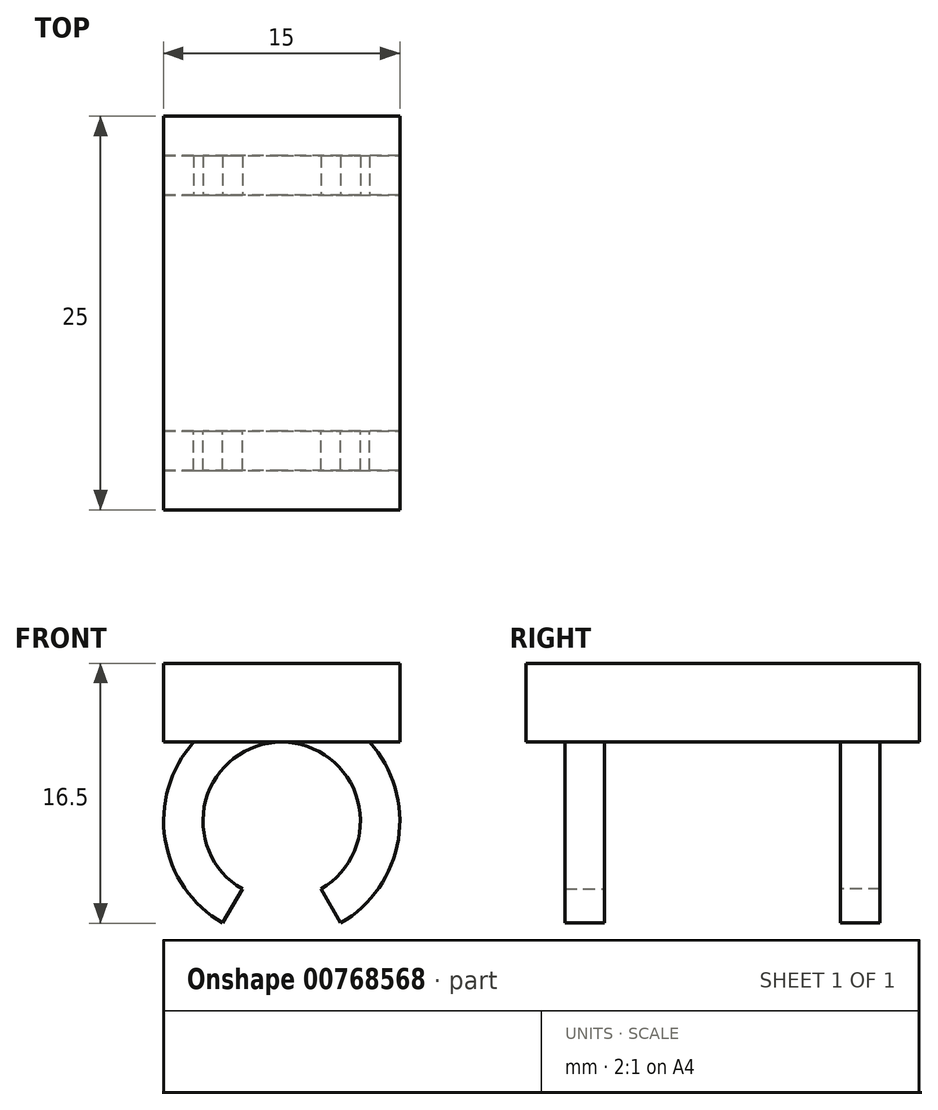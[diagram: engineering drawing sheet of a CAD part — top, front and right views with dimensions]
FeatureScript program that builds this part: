
annotation { "Feature Type Name" : "Feature", "Feature Type Description" : "" }
export const myFeature = defineFeature(function(context is Context, id is Id, definition is map)
    precondition{}
    {
        {
            var Q0;
            Q0=qCreatedBy(makeId("Front.planeOp"),FACE);
            var sketch = newSketch(context, id + "F0", { "sketchPlane" : qUnion([Q0])});
            skLineSegment(sketch, "E0.bottom", {"start": v(-7.5, 2.5) * mm, "end": v(7.5, 2.5) * mm});
            skLineSegment(sketch, "E0.top", {"start": v(-7.5, -2.5) * mm, "end": v(7.5, -2.5) * mm});
            skLineSegment(sketch, "E0.left", {"start": v(-7.5, 2.5) * mm, "end": v(-7.5, -2.5) * mm});
            skLineSegment(sketch, "E0.right", {"start": v(7.5, 2.5) * mm, "end": v(7.5, -2.5) * mm});
            skPoint(sketch, "E0.middle", {"position": v(0, 0) * mm});
            skCircle(sketch, "E1", {"center": v(0, -7.5) * mm, "radius": 5 * mm});
            skCircle(sketch, "E2", {"center": v(0, -7.5) * mm, "radius": 7.5 * mm});
            skLineSegment(sketch, "E3", {"start": v(2.5, -11.83) * mm, "end": v(3.75, -14) * mm});
            skLineSegment(sketch, "E4", {"start": v(-2.5, -11.83) * mm, "end": v(-3.75, -14) * mm});
            skSolve(sketch);
        }
        {
            var Q0;
            Q0=makeQuery(id+"F0.imprint","IMPRINT",FACE,{"disambiguationData":[TD([[makeQuery(id+"F0.imprint","IMPRINT",EDGE,{"derivedFrom":sQuery(id+"F0.wireOp",EDGE,"E0.bottom")}),-1.0]])]});
            var Q1;
            {var subQ0=sQuery(id+"F0.wireOp",EDGE,"E2");var subQ1=sQuery(id+"F0.wireOp",EDGE,"E0.top");var subQ2=makeQuery(id+"F0.imprint","INTERSECT",VERTEX,{"disambiguationData":[OD(0.0)],"derivedFrom":[subQ1,subQ0]});Q1=makeQuery(id+"F0.imprint","IMPRINT",FACE,{"disambiguationData":[TD([[makeQuery(id+"F0.imprint","IMPRINT",EDGE,{"disambiguationData":[TD([[subQ2,-1.0]])],"derivedFrom":subQ1}),1.0]])]});}
            extrude(context, id + "F1", {"entities" : qUnion([Q0, Q1]), "endBound" : BoundingType.SYMMETRIC, "depth" : 25 * mm, "offsetDistance" : 25 * mm});
        }
        {
            var Q0;
            {var subQ5=sQuery(id+"F0.wireOp",EDGE,"E4");Q0=makeQuery(id+"F0.imprint","IMPRINT",FACE,{"disambiguationData":[TD([[makeQuery(id+"F0.imprint","IMPRINT",EDGE,{"derivedFrom":subQ5}),-1.0]])]});}
            var Q1;
            {var subQ5=sQuery(id+"F0.wireOp",EDGE,"E3");Q1=makeQuery(id+"F0.imprint","IMPRINT",FACE,{"disambiguationData":[TD([[makeQuery(id+"F0.imprint","IMPRINT",EDGE,{"derivedFrom":subQ5}),1.0]])]});}
            extrude(context, id + "F2", {"entities" : qUnion([Q0, Q1]), "operationType" : NewBodyOperationType.ADD, "depth" : 10 * mm, "offsetDistance" : 25 * mm, "hasSecondDirection" : true, "secondDirectionOppositeDirection" : true, "secondDirectionDepth" : -7.5 * mm});
        }
        {
            var Q0;
            {var subQ5=sQuery(id+"F0.wireOp",EDGE,"E3");Q0=makeQuery(id+"F0.imprint","IMPRINT",FACE,{"disambiguationData":[TD([[makeQuery(id+"F0.imprint","IMPRINT",EDGE,{"derivedFrom":subQ5}),1.0]])]});}
            var Q1;
            {var subQ5=sQuery(id+"F0.wireOp",EDGE,"E4");Q1=makeQuery(id+"F0.imprint","IMPRINT",FACE,{"disambiguationData":[TD([[makeQuery(id+"F0.imprint","IMPRINT",EDGE,{"derivedFrom":subQ5}),-1.0]])]});}
            extrude(context, id + "F3", {"entities" : qUnion([Q0, Q1]), "operationType" : NewBodyOperationType.ADD, "oppositeDirection" : true, "depth" : 10 * mm, "offsetDistance" : 25 * mm, "hasSecondDirection" : true, "secondDirectionOppositeDirection" : false, "secondDirectionDepth" : -7.5 * mm});
        }
    });
